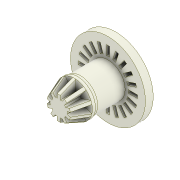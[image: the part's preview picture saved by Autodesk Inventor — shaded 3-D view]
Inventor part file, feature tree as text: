
AUTODESK INVENTOR PART (.ipt)
format: ipt  version: 2022 (Build 260153000, 153)  size: 365,568 bytes
history: native  units: mm
features: extrude x8, sketch x7, thicken_offset x2, chamfer x1, pattern_circular x1, fillet x1, plane x1, other x1
ambient origin geometry x8: Origin, YZ Plane, XZ Plane, XY Plane, X Axis, Y Axis, Z Axis, Center Point
bodies: Solid1 (feature_tree)
feature tree (22):
  extrude  "Adapter"  Depth=1.0mm TaperAngle=0.0deg
  extrude  "Motor Shaft Profile"  Depth=6.0mm
  chamfer  "Chamfer1"  Distance=12.0mm
  thicken_offset  "Thicken5"
  thicken_offset  "Thicken6"
  extrude  "Extrusion5"  Depth=2.0mm TaperAngle=45.0deg
  extrude  "Extrusion6"  Depth=0.15mm
  extrude  "Extrusion7"  Depth=7.5mm
  pattern_circular  "Circular Pattern1"  [2 undecoded]
  extrude  "Extrusion8"  TaperAngle=0.0deg  [1 undecoded]
  fillet  "Fillet1"  Radius=100.0mm
  plane  "Work Plane1"
  extrude  "Extrusion9"  Depth=5.0mm
  extrude  "Extrusion10"  Depth=10.0mm TaperAngle=0.0deg
  sketch  "Sketch1"  dims[d1=11.0mm d2=1.0mm d3=0.0mm]
  sketch  "Sketch6"  dims[d4=13.0mm d5=0.0mm d35=6.0mm]
  sketch  "Sketch10"  dims[d36=5.5mm d37=12.0mm d38=0.0mm]
  sketch  "Sketch11"  dims[d39=0.15mm d40=0.1mm d48=0.5mm d49=2.0mm d50=45.0deg]
  sketch  "Sketch12"  dims[d58=0.15mm d59=0.2mm d74=11.5mm]
  sketch  "Sketch13"  dims[d75=1.0mm d76=0.0mm d77=7.5mm]
  other  "Encoder Wheel"
  sketch  "Sketch15"  dims[d78=6.0mm d79=1.0mm d80=0.0mm d81=0.0mm d82=0.0mm d83=100.0mm d84=360.0deg d86=5.0mm d87=10.0mm d88=0.0mm d89=2.0mm d90=24.0mm d91=2.5mm d92=0.0mm d93=1.0mm d94=9.5mm d95=6.5mm d96=200.0mm d98=360.0deg d100=0.0mm d101=0.0mm d102=-1.75mm d41=1.0mm d42=1.0mm d43=1.0mm d44=0.15mm d45=0.25mm d46=0.375mm d47=14.3117mm d51=0.75mm d52=0.375mm d60=0.5mm d61=0.872665mm]
note: 3 required parameter values undecoded (feature->parameter linkage not recoverable at this tier; creation-order binding heuristic only, values carry confidence <= 0.55)
